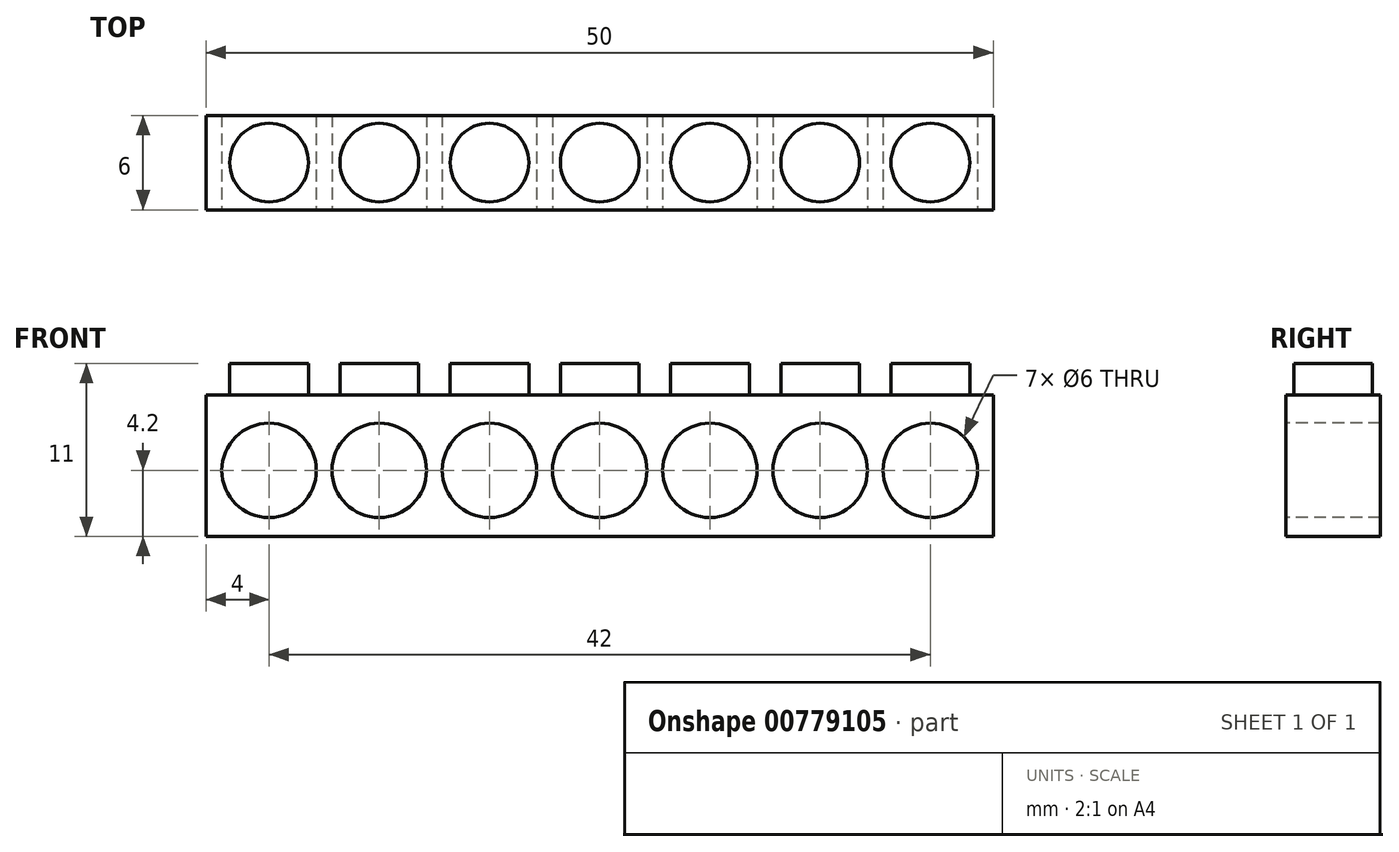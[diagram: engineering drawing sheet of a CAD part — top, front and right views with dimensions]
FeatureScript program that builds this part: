
annotation { "Feature Type Name" : "Feature", "Feature Type Description" : "" }
export const myFeature = defineFeature(function(context is Context, id is Id, definition is map)
    precondition{}
    {
        {
            var Q0;
            Q0=qCreatedBy(makeId("Front.planeOp"),FACE);
            var sketch = newSketch(context, id + "F0", { "sketchPlane" : qUnion([Q0])});
            skLineSegment(sketch, "E0.bottom", {"start": v(0, 0) * mm, "end": v(50, 0) * mm});
            skLineSegment(sketch, "E0.top", {"start": v(0, 9) * mm, "end": v(50, 9) * mm});
            skLineSegment(sketch, "E0.left", {"start": v(0, 0) * mm, "end": v(0, 9) * mm});
            skLineSegment(sketch, "E0.right", {"start": v(50, 0) * mm, "end": v(50, 9) * mm});
            skSolve(sketch);
        }
        {
            var Q0;
            Q0=makeQuery(id+"F0.imprint","IMPRINT",FACE,{"disambiguationData":[TD([[makeQuery(id+"F0.imprint","IMPRINT",EDGE,{"derivedFrom":sQuery(id+"F0.wireOp",EDGE,"E0.bottom")}),1.0]])]});
            extrude(context, id + "F1", {"entities" : qUnion([Q0]), "depth" : 6 * mm, "offsetDistance" : 25 * mm});
        }
        {
            var Q0;
            Q0=makeQuery(id+"F1.opExtrude","CAP_FACE",FACE,{"disambiguationData":[OSD([sQuery(id+"F0.wireOp",EDGE,"E0.bottom"),sQuery(id+"F0.wireOp",EDGE,"E0.top"),sQuery(id+"F0.wireOp",EDGE,"E0.left"),sQuery(id+"F0.wireOp",EDGE,"E0.right")])],"isStart":false});
            var sketch = newSketch(context, id + "F2", { "sketchPlane" : qUnion([Q0])});
            skCircle(sketch, "E1", {"center": v(25, 4.2) * mm, "radius": 3 * mm});
            skCircle(sketch, "E2.1.0.0", {"center": v(32, 4.2) * mm, "radius": 3 * mm});
            skCircle(sketch, "E2.2.0.0", {"center": v(39, 4.2) * mm, "radius": 3 * mm});
            skLineSegment(sketch, "E2.direction1", {"start": v(25, 4.2) * mm, "end": v(32, 4.2) * mm, "construction": true});
            skCircle(sketch, "E3.0.3.0", {"center": v(46, 4.2) * mm, "radius": 3 * mm});
            skCircle(sketch, "E4.1.0.0", {"center": v(18, 4.2) * mm, "radius": 3 * mm});
            skCircle(sketch, "E4.2.0.0", {"center": v(11, 4.2) * mm, "radius": 3 * mm});
            skCircle(sketch, "E4.3.0.0", {"center": v(4, 4.2) * mm, "radius": 3 * mm});
            skLineSegment(sketch, "E4.direction1", {"start": v(25, 4.2) * mm, "end": v(18, 4.2) * mm, "construction": true});
            skSolve(sketch);
        }
        {
            var Q0;
            Q0=makeQuery(id+"F2.imprint","IMPRINT",FACE,{"disambiguationData":[TD([[makeQuery(id+"F2.imprint","IMPRINT",EDGE,{"derivedFrom":sQuery(id+"F2.wireOp",EDGE,"E4.3.0.0")}),1.0]])]});
            var Q1;
            Q1=makeQuery(id+"F2.imprint","IMPRINT",FACE,{"disambiguationData":[TD([[makeQuery(id+"F2.imprint","IMPRINT",EDGE,{"derivedFrom":sQuery(id+"F2.wireOp",EDGE,"E4.2.0.0")}),1.0]])]});
            var Q2;
            Q2=makeQuery(id+"F2.imprint","IMPRINT",FACE,{"disambiguationData":[TD([[makeQuery(id+"F2.imprint","IMPRINT",EDGE,{"derivedFrom":sQuery(id+"F2.wireOp",EDGE,"E4.1.0.0")}),1.0]])]});
            var Q3;
            Q3=makeQuery(id+"F2.imprint","IMPRINT",FACE,{"disambiguationData":[TD([[makeQuery(id+"F2.imprint","IMPRINT",EDGE,{"derivedFrom":sQuery(id+"F2.wireOp",EDGE,"E1")}),1.0]])]});
            var Q4;
            Q4=makeQuery(id+"F2.imprint","IMPRINT",FACE,{"disambiguationData":[TD([[makeQuery(id+"F2.imprint","IMPRINT",EDGE,{"derivedFrom":sQuery(id+"F2.wireOp",EDGE,"E2.1.0.0")}),1.0]])]});
            var Q5;
            Q5=makeQuery(id+"F2.imprint","IMPRINT",FACE,{"disambiguationData":[TD([[makeQuery(id+"F2.imprint","IMPRINT",EDGE,{"derivedFrom":sQuery(id+"F2.wireOp",EDGE,"E2.2.0.0")}),1.0]])]});
            var Q6;
            Q6=makeQuery(id+"F2.imprint","IMPRINT",FACE,{"disambiguationData":[TD([[makeQuery(id+"F2.imprint","IMPRINT",EDGE,{"derivedFrom":sQuery(id+"F2.wireOp",EDGE,"E3.0.3.0")}),1.0]])]});
            extrude(context, id + "F3", {"entities" : qUnion([Q0, Q1, Q2, Q3, Q4, Q5, Q6]), "operationType" : NewBodyOperationType.REMOVE, "oppositeDirection" : true, "depth" : 25 * mm, "offsetDistance" : 25 * mm});
        }
        {
            var Q0;
            Q0=makeQuery(id+"F1.opExtrude","SWEPT_FACE",FACE,{"disambiguationData":[OSD([sQuery(id+"F0.wireOp",EDGE,"E0.top")])]});
            var sketch = newSketch(context, id + "F4", { "sketchPlane" : qUnion([Q0])});
            skLineSegment(sketch, "E5", {"start": v(25, 0) * mm, "end": v(25, -6) * mm});
            skCircle(sketch, "E6", {"center": v(25, -3) * mm, "radius": 2.5 * mm});
            skCircle(sketch, "E7.1.0.0", {"center": v(32, -3) * mm, "radius": 2.5 * mm});
            skCircle(sketch, "E7.2.0.0", {"center": v(39, -3) * mm, "radius": 2.5 * mm});
            skCircle(sketch, "E7.3.0.0", {"center": v(46, -3) * mm, "radius": 2.5 * mm});
            skLineSegment(sketch, "E7.direction1", {"start": v(25, -3) * mm, "end": v(32, -3) * mm, "construction": true});
            skCircle(sketch, "E8.1.0.0", {"center": v(18, -3) * mm, "radius": 2.5 * mm});
            skCircle(sketch, "E8.2.0.0", {"center": v(11, -3) * mm, "radius": 2.5 * mm});
            skCircle(sketch, "E8.3.0.0", {"center": v(4, -3) * mm, "radius": 2.5 * mm});
            skLineSegment(sketch, "E8.direction1", {"start": v(25, -3) * mm, "end": v(18, -3) * mm, "construction": true});
            skSolve(sketch);
        }
        {
            var Q0;
            Q0=makeQuery(id+"F4.imprint","IMPRINT",FACE,{"disambiguationData":[TD([[makeQuery(id+"F4.imprint","IMPRINT",EDGE,{"derivedFrom":sQuery(id+"F4.wireOp",EDGE,"E8.3.0.0")}),1.0]])]});
            var Q1;
            Q1=makeQuery(id+"F4.imprint","IMPRINT",FACE,{"disambiguationData":[TD([[makeQuery(id+"F4.imprint","IMPRINT",EDGE,{"derivedFrom":sQuery(id+"F4.wireOp",EDGE,"E8.2.0.0")}),1.0]])]});
            var Q2;
            Q2=makeQuery(id+"F4.imprint","IMPRINT",FACE,{"disambiguationData":[TD([[makeQuery(id+"F4.imprint","IMPRINT",EDGE,{"derivedFrom":sQuery(id+"F4.wireOp",EDGE,"E8.1.0.0")}),1.0]])]});
            var Q3;
            {var subQ0=sQuery(id+"F4.wireOp",EDGE,"E6");var subQ1=sQuery(id+"F4.wireOp",EDGE,"E5");var subQ2=makeQuery(id+"F4.imprint","INTERSECT",VERTEX,{"disambiguationData":[OD(0.0)],"derivedFrom":[subQ1,subQ0]});Q3=makeQuery(id+"F4.imprint","IMPRINT",FACE,{"disambiguationData":[TD([[makeQuery(id+"F4.imprint","IMPRINT",EDGE,{"disambiguationData":[TD([[subQ2,-1.0]])],"derivedFrom":subQ1}),1.0]])]});}
            var Q4;
            {var subQ0=sQuery(id+"F4.wireOp",EDGE,"E6");var subQ1=sQuery(id+"F4.wireOp",EDGE,"E5");var subQ2=makeQuery(id+"F4.imprint","INTERSECT",VERTEX,{"disambiguationData":[OD(0.0)],"derivedFrom":[subQ1,subQ0]});Q4=makeQuery(id+"F4.imprint","IMPRINT",FACE,{"disambiguationData":[TD([[makeQuery(id+"F4.imprint","IMPRINT",EDGE,{"disambiguationData":[TD([[subQ2,-1.0]])],"derivedFrom":subQ1}),-1.0]])]});}
            var Q5;
            Q5=makeQuery(id+"F4.imprint","IMPRINT",FACE,{"disambiguationData":[TD([[makeQuery(id+"F4.imprint","IMPRINT",EDGE,{"derivedFrom":sQuery(id+"F4.wireOp",EDGE,"E7.1.0.0")}),1.0]])]});
            var Q6;
            Q6=makeQuery(id+"F4.imprint","IMPRINT",FACE,{"disambiguationData":[TD([[makeQuery(id+"F4.imprint","IMPRINT",EDGE,{"derivedFrom":sQuery(id+"F4.wireOp",EDGE,"E7.2.0.0")}),1.0]])]});
            var Q7;
            Q7=makeQuery(id+"F4.imprint","IMPRINT",FACE,{"disambiguationData":[TD([[makeQuery(id+"F4.imprint","IMPRINT",EDGE,{"derivedFrom":sQuery(id+"F4.wireOp",EDGE,"E7.3.0.0")}),1.0]])]});
            extrude(context, id + "F5", {"entities" : qUnion([Q0, Q1, Q2, Q3, Q4, Q5, Q6, Q7]), "operationType" : NewBodyOperationType.ADD, "depth" : 2 * mm, "offsetDistance" : 25 * mm});
        }
    });
